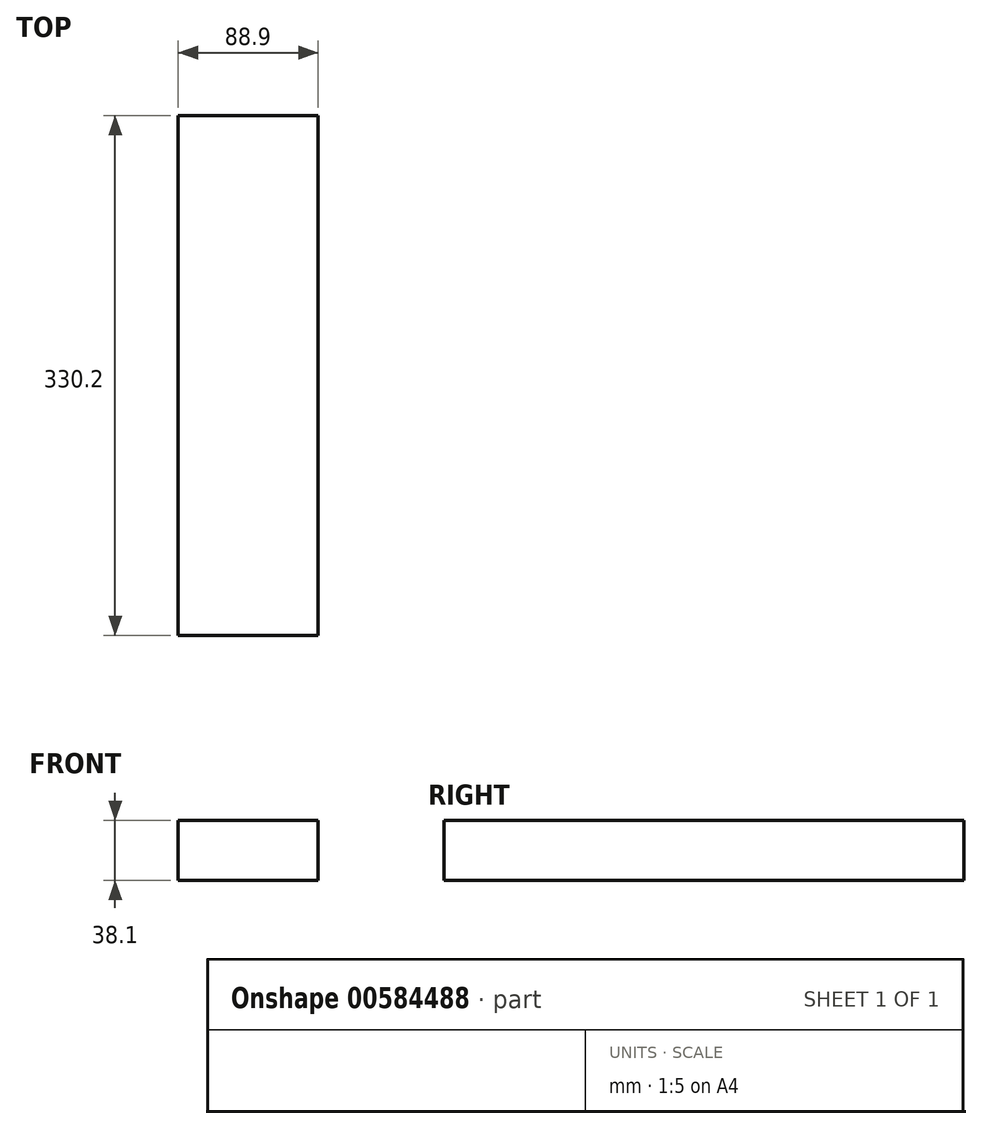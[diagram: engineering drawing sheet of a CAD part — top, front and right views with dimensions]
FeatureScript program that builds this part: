
annotation { "Feature Type Name" : "Feature", "Feature Type Description" : "" }
export const myFeature = defineFeature(function(context is Context, id is Id, definition is map)
    precondition{}
    {
        {
            var Q0;
            Q0=qCreatedBy(makeId("Front.planeOp"),FACE);
            var sketch = newSketch(context, id + "F0", { "sketchPlane" : qUnion([Q0])});
            skLineSegment(sketch, "E0.bottom", {"start": v(0, 0) * mm, "end": v(88.9, 0) * mm});
            skLineSegment(sketch, "E0.top", {"start": v(0, 38.1) * mm, "end": v(88.9, 38.1) * mm});
            skLineSegment(sketch, "E0.left", {"start": v(0, 0) * mm, "end": v(0, 38.1) * mm});
            skLineSegment(sketch, "E0.right", {"start": v(88.9, 0) * mm, "end": v(88.9, 38.1) * mm});
            skSolve(sketch);
        }
        {
            var Q0;
            Q0=makeQuery(id+"F0.imprint","IMPRINT",FACE,{"disambiguationData":[TD([[makeQuery(id+"F0.imprint","IMPRINT",EDGE,{"derivedFrom":sQuery(id+"F0.wireOp",EDGE,"E0.bottom")}),1.0]])]});
            extrude(context, id + "F1", {"entities" : qUnion([Q0]), "depth" : 330.2 * mm, "offsetDistance" : 25.4 * mm});
        }
    });
